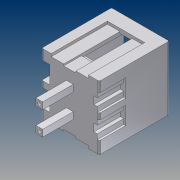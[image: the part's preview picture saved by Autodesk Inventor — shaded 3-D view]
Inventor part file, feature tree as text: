
AUTODESK INVENTOR PART (.ipt)
format: ipt  version: 2012 (Build 160160000, 160)  size: 226,816 bytes
history: native  units: mm (DEFAULTED — no unit token found)
features: sketch x16, extrude x15, pattern_linear x4, projected_geometry x2, other x1
ambient origin geometry x8: Origin, YZ Plane, XZ Plane, XY Plane, X Axis, Y Axis, Z Axis, Center Point
bodies: Solid1 (feature_tree)
feature tree (38):
  extrude  "Extrusion1"  Depth=7.5mm TaperAngle=0.0deg
  extrude  "Extrusion2"  Depth=7.7mm TaperAngle=0.0deg
  extrude  "Extrusion3"  Depth=6.0mm TaperAngle=0.0deg
  extrude  "Extrusion4"  Depth=20.0mm TaperAngle=0.0deg
  extrude  "Extrusion5"  Depth=20.0mm TaperAngle=0.0deg
  extrude  "Extrusion6"  Depth=20.0mm TaperAngle=0.0deg
  extrude  "Extrusion7"  Depth=8.3mm TaperAngle=0.0deg
  pattern_linear  "Rectangular Pattern1"  Count1=2 Spacing1=3.5mm
  extrude  "Extrusion8"  Depth=3.9mm TaperAngle=0.0deg
  pattern_linear  "Rectangular Pattern2"  [2 undecoded]
  extrude  "Extrusion9"  [1 undecoded]
  pattern_linear  "Rectangular Pattern3"  [2 undecoded]
  extrude  "Extrusion10"  [1 undecoded]
  extrude  "Extrusion11"  [1 undecoded]
  extrude  "Extrusion12"  [1 undecoded]
  pattern_linear  "Rectangular Pattern4"  [2 undecoded]
  extrude  "Extrusion13"  [1 undecoded]
  extrude  "Extrusion14"  [1 undecoded]
  sketch  "Sketch15"
  other  "Work Axis1"
  extrude  "Extrusion15"  [1 undecoded]
  sketch  "Skizze_1"  dims[d0=9.4mm d1=0.0mm d2=7.5mm d3=0.0mm]
  sketch  "Skizze_2"  dims[d4=7.7mm d5=0.0mm d6=7.7mm d7=0.0mm]
  sketch  "Skizze_3"  dims[d8=6.0mm d9=0.0mm d10=6.0mm d11=0.0mm]
  sketch  "Skizze_4"  dims[d12=3.6mm d13=0.0mm d14=20.0mm d16=3.5mm d17=10.0mm d19=0.0mm]
  sketch  "Skizze_5"  dims[d20=9.3mm d21=0.0mm d22=20.0mm d24=3.5mm d25=10.0mm d27=0.0mm]
  sketch  "Skizze_6"  dims[d28=4.5mm d29=0.0mm d30=20.0mm d32=3.5mm d33=10.0mm d35=0.0mm]
  sketch  "Skizze_7"  dims[d36=8.3mm d37=0.0mm d38=8.3mm d39=0.0mm]
  sketch  "Skizze_9"  dims[d40=9.15mm d41=0.0mm d42=20.0mm d44=3.5mm d45=10.0mm d47=0.0mm]
  sketch  "Skizze_11"  dims[d48=3.9mm d49=0.0mm d50=3.9mm d51=0.0mm]
  sketch  "Skizze_13"  dims[d52=0.5mm]
  sketch  "Skizze_14"  dims[d53=10.0mm d54=0.0mm]
  sketch  "Skizze_15"
  sketch  "Skizze_17"
  sketch  "Skizze_18"
  sketch  "Sketch16"
  projected_geometry  "Projected Loop1"
  projected_geometry  "Projected Loop2"
note: 13 required parameter values undecoded (feature->parameter linkage not recoverable at this tier; creation-order binding heuristic only, values carry confidence <= 0.55)
